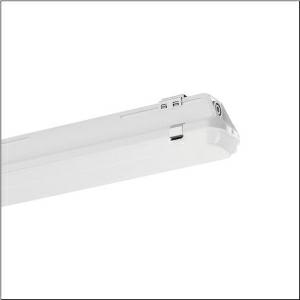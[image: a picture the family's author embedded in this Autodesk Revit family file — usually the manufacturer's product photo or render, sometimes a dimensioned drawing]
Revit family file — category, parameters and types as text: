
# Revit family: monsun_r__11_51fp10dp480l_6cbf
name_source: partatom
category: Lighting Fixtures
units: mm (PartAtom-declared; Revit-internal decimal feet)

## family parameters
Cut with Voids When Loaded = No
Host = Face
Light Source = No
Part Type = Normal
Room Calculation Point = No
Round Connector Dimension = Use Diameter
Shared = No

## types (1)
- --- (1 x LED, 8000 lm, 44.4 W, 4000K)
    Apparent Load = 44 VA
    CIE Flux Codes = 47 77 93 94 100
    Color Rendering = 80
    Color Temperature = 4000K
    Default Elevation = 1800 mm
    Description = Monsun® 11, damp-proof luminaire, chain hanger, primary optical cover: enclosure, of PMMA, light emission: direct distribution, primary light characteristic: symmetric, installation type: suspended mounting, surface-mounted, horizontal mounting, vertical mounting, LED, rated luminous flux: 8.000lm, luminous efficacy: 180lm/W, light colour: 840, colour temperature: 4000K, control gear: DALI 2, with terminal, 5-pole, max. 2.5mm², mains connection: 220..240V, AC, 50/60Hz, rated input power: 44W, luminaire housing, of glass-fibre reinforced polyester, uncoated, bright grey, incl. chain hanger, length: 1.590mm, width: 90mm, height: 88mm, clip for enclosure, of stainless steel (V2A), ceiling mounting element, of stainless steel (V2A), chain hanger, of stainless steel (V2A), protection rating (complete): IP66, insulation class (complete): insulation class I (protective earthing), certification: CE, ENEC, VDE, UKCA, protection symbol: D, impact resistance: IK04, permissible operating ambient temperature: -25..+40°C, standard: EN 50419, EN 60598-2-1, corresponds to IFS (International Featured Standards) requirements for safety and quality in the food industry, for indoor or canopied outdoor use, no direct snow, no direct sun, no direct rain, LABS conformity tested according to VDMA 24364:2018-05, contact your sales advisor before using the luminaires in applications with unclear chemical exposure, large temperature fluctuations or condensation-forming humidity, packaging unit: 1 piece
    Height = 89 mm
    Lamp = 1 x LED
    Lamp Light Flux = 8000 lm
    Lamp Power = 44.4 W
    Lamp count = 1
    Length = 1590 mm
    Luminous efficacy = 180 lm/W
    Manufacturer = Siteco
    ModVariant = No
    Model = 51FP10DP480L
    Mounting Place = Ceiling
    Mounting Type = Surface mounted
    Number of Poles = 1
    OnlyDefault = Yes
    Power Factor = 1
    Product Name = Monsun® 11
    Product group = damp-proof luminaire
    ProductGroupID = 300
    Protection Class = Protection class I
    Protection Degree = IP 66
    RLX_Detail_Level = 1
    RLX_Emergency_Light_Flux = 0 lm
    RLX_Emergency_Type = 0
    RLX_Emergency_Type_DB = No
    RlxData = <blob elided: 91673 chars, md5=0dfecf6c>
    Socket = socket
    Standby Power = 0 W
    System Light Flux = 8000 lm
    System Power = 44 W
    Type Comments = factory setting: luminous flux: 100 % | dim-lin: 254 | 295 mA
    Type Image = l_1349237.jpg
    URL = http://relux.com
    VarID = @adj_018010
    Voltage = 0 V
    Weight = 0.00 kg
    Width = 90 mm

## geometry (parser evidence)
native form markers: Blend x4, Sweep x14
no freeform markers — native parametric forms only
